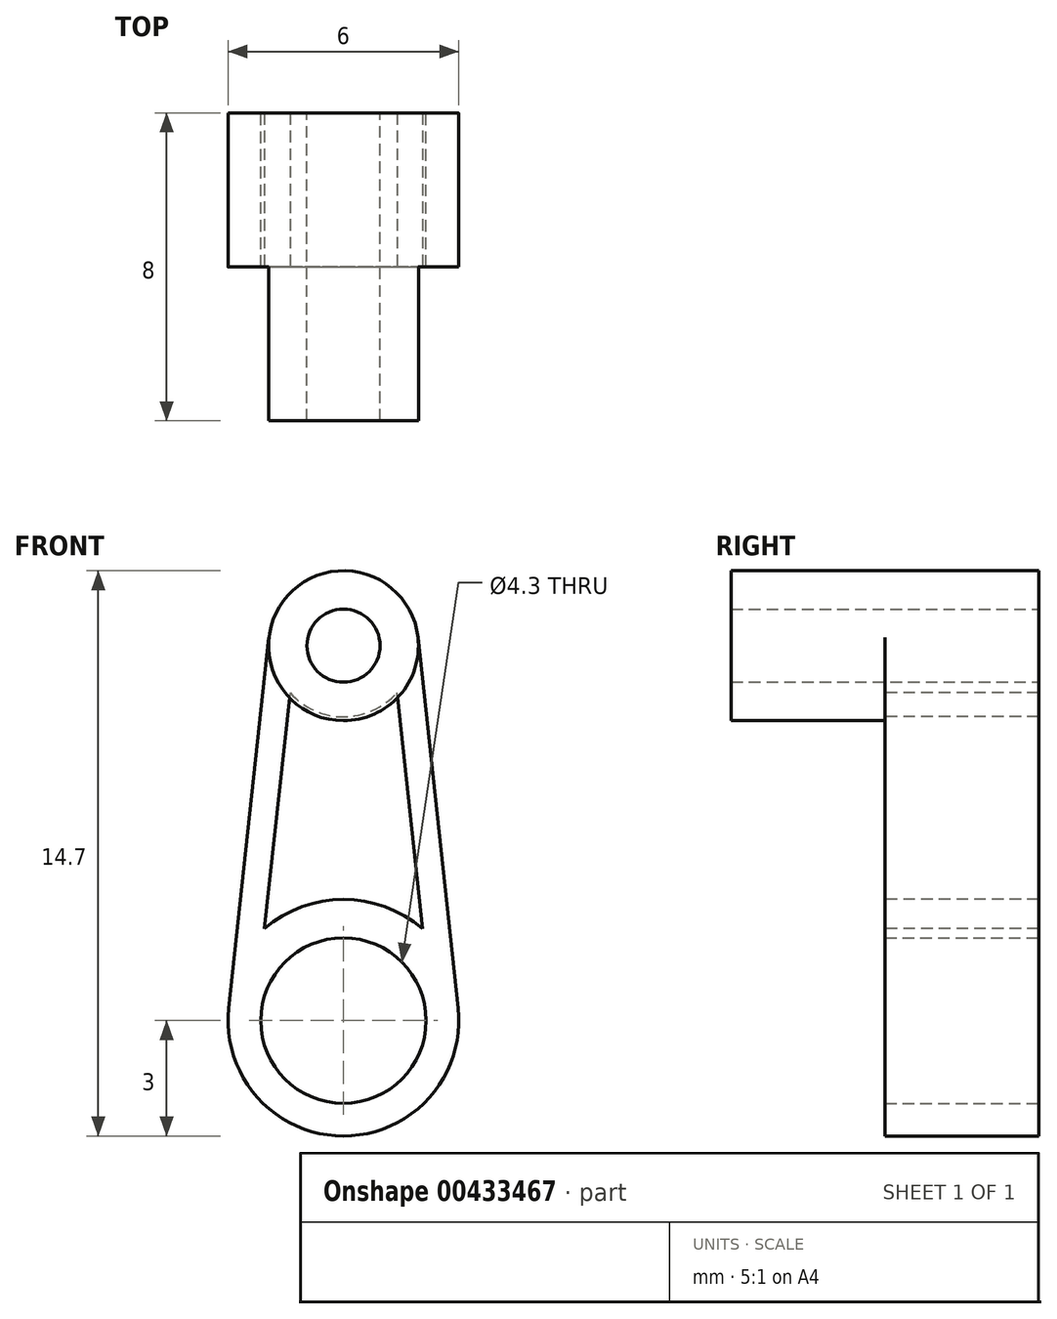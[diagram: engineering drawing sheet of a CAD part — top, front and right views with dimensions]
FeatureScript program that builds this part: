
annotation { "Feature Type Name" : "Feature", "Feature Type Description" : "" }
export const myFeature = defineFeature(function(context is Context, id is Id, definition is map)
    precondition{}
    {
        {
            var Q0;
            Q0=qCreatedBy(makeId("Front.planeOp"),FACE);
            var sketch = newSketch(context, id + "F0", { "sketchPlane" : qUnion([Q0])});
            skArc(sketch, "E0", {"start": v(-2.98, 0.32) * mm, "mid": v(0, -3) * mm, "end": v(2.98, 0.32) * mm});
            skArc(sketch, "E1", {"start": v(1.94, 9.96) * mm, "mid": v(0, 11.7) * mm, "end": v(-1.94, 9.96) * mm});
            skLineSegment(sketch, "E2", {"start": v(-1.94, 9.96) * mm, "end": v(-2.98, 0.32) * mm});
            skLineSegment(sketch, "E3", {"start": v(2.98, 0.32) * mm, "end": v(1.94, 9.96) * mm});
            skCircle(sketch, "E4", {"center": v(0, 9.75) * mm, "radius": 0.95 * mm});
            skCircle(sketch, "E5", {"center": v(0, 0) * mm, "radius": 2.15 * mm});
            skSolve(sketch);
        }
        {
            var Q0;
            Q0=qSketchRegion(id+"F0",true);
            extrude(context, id + "F1", {"entities" : qUnion([Q0]), "depth" : 4 * mm});
        }
        {
            var Q0;
            Q0=makeQuery(id+"F1.opExtrude","CAP_FACE",FACE,{"disambiguationData":[OSD([sQuery(id+"F0.wireOp",EDGE,"E0"),sQuery(id+"F0.wireOp",EDGE,"E1"),sQuery(id+"F0.wireOp",EDGE,"E2"),sQuery(id+"F0.wireOp",EDGE,"E3"),sQuery(id+"F0.wireOp",EDGE,"E4"),sQuery(id+"F0.wireOp",EDGE,"E5")])],"isStart":false});
            var sketch = newSketch(context, id + "F2", { "sketchPlane" : qUnion([Q0])});
            skLineSegment(sketch, "E6.0", {"start": v(-1.39, 8.53) * mm, "end": v(-2.05, 2.39) * mm});
            skLineSegment(sketch, "E7.0", {"start": v(2.05, 2.39) * mm, "end": v(1.39, 8.53) * mm});
            skArc(sketch, "E8.0", {"start": v(-1.39, 8.53) * mm, "mid": v(0, 7.9) * mm, "end": v(1.39, 8.53) * mm});
            skArc(sketch, "E9.0", {"start": v(2.05, 2.39) * mm, "mid": v(0, 3.15) * mm, "end": v(-2.05, 2.39) * mm});
            skSolve(sketch);
        }
        {
            var Q0;
            Q0=qSketchRegion(id+"F2",true);
            extrude(context, id + "F3", {"entities" : qUnion([Q0]), "operationType" : NewBodyOperationType.REMOVE, "oppositeDirection" : true, "depth" : 25 * mm});
        }
        {
            var Q0;
            Q0=makeQuery(id+"F1.opExtrude","CAP_FACE",FACE,{"disambiguationData":[OSD([sQuery(id+"F0.wireOp",EDGE,"E0"),sQuery(id+"F0.wireOp",EDGE,"E1"),sQuery(id+"F0.wireOp",EDGE,"E2"),sQuery(id+"F0.wireOp",EDGE,"E3"),sQuery(id+"F0.wireOp",EDGE,"E4"),sQuery(id+"F0.wireOp",EDGE,"E5")])],"isStart":false});
            var sketch = newSketch(context, id + "F4", { "sketchPlane" : qUnion([Q0])});
            skCircle(sketch, "E10", {"center": v(0, 9.75) * mm, "radius": 0.95 * mm});
            skCircle(sketch, "E11", {"center": v(0, 9.75) * mm, "radius": 1.95 * mm});
            skSolve(sketch);
        }
        {
            var Q0;
            Q0=qSketchRegion(id+"F4",true);
            extrude(context, id + "F5", {"entities" : qUnion([Q0]), "operationType" : NewBodyOperationType.ADD, "depth" : 4 * mm});
        }
    });
